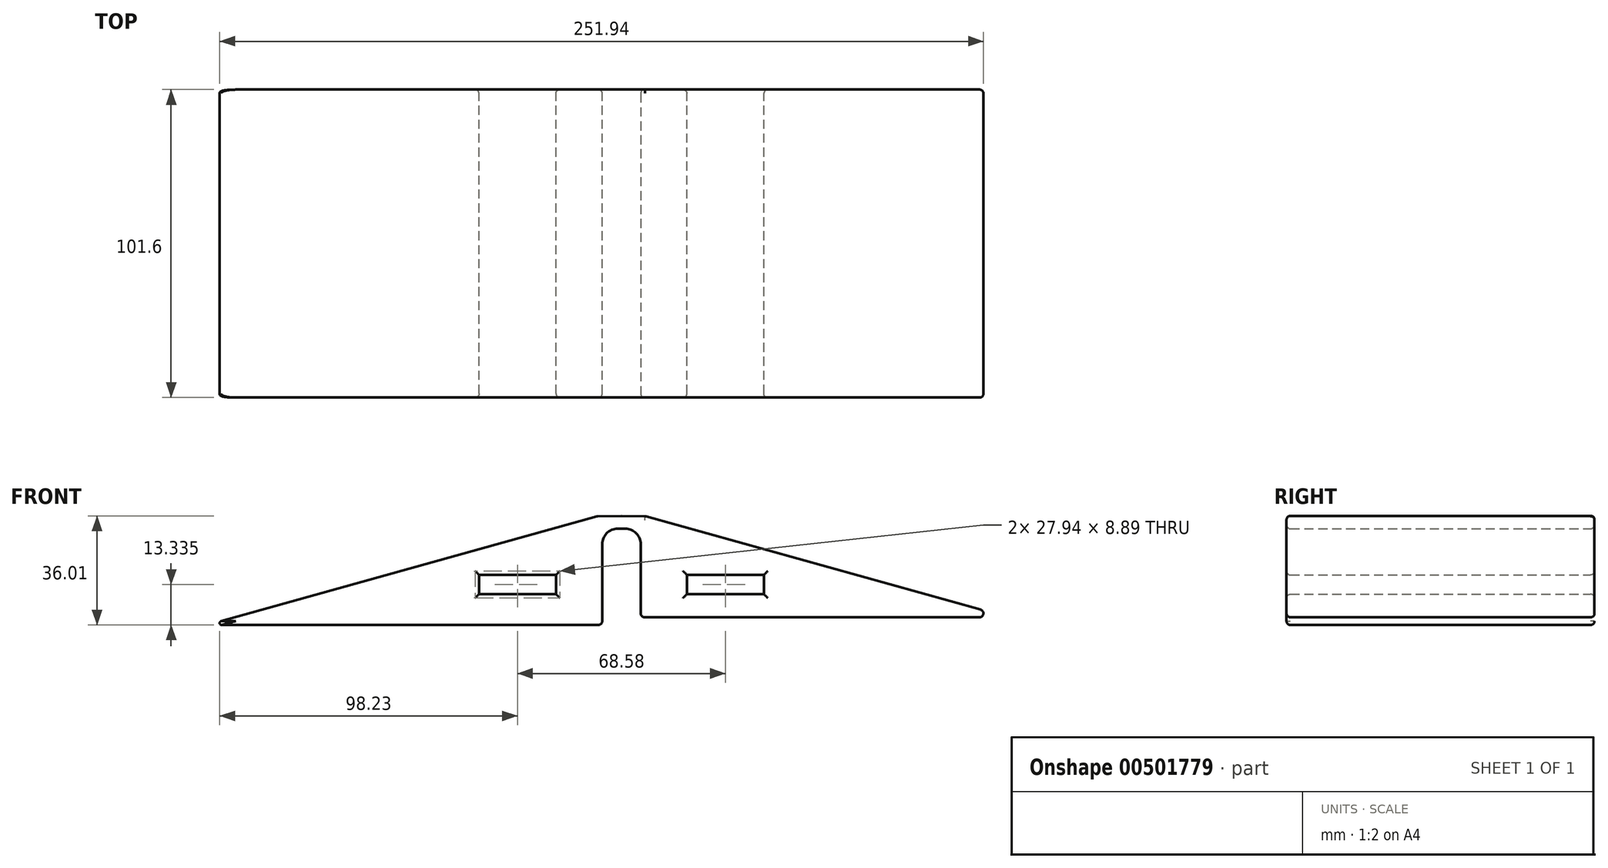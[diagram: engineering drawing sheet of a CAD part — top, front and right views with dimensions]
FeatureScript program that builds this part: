
annotation { "Feature Type Name" : "Feature", "Feature Type Description" : "" }
export const myFeature = defineFeature(function(context is Context, id is Id, definition is map)
    precondition{}
    {
        {
            var Q0;
            Q0=qCreatedBy(makeId("Front.planeOp"),FACE);
            var sketch = newSketch(context, id + "F0", { "sketchPlane" : qUnion([Q0])});
            skLineSegment(sketch, "E0", {"start": v(-6.35, 0) * mm, "end": v(-136.53, 0) * mm});
            skLineSegment(sketch, "E1", {"start": v(-136.53, 0) * mm, "end": v(-7.96, 35.88) * mm});
            skLineSegment(sketch, "E2", {"start": v(0, 36) * mm, "end": v(0, 31.75) * mm});
            skLineSegment(sketch, "E3", {"start": v(-6.35, 0) * mm, "end": v(-6.35, 31.75) * mm});
            skLineSegment(sketch, "E4", {"start": v(-6.35, 31.75) * mm, "end": v(0, 31.75) * mm});
            skLineSegment(sketch, "E5", {"start": v(0, 36) * mm, "end": v(-7.96, 35.88) * mm});
            skPoint(sketch, "E6.orphan", {"position": v(0, 38.1) * mm});
            skPoint(sketch, "E7.orphan", {"position": v(0, 0) * mm});
            skLineSegment(sketch, "E8.bottom", {"start": v(-21.59, 10.16) * mm, "end": v(-47, 10.16) * mm});
            skLineSegment(sketch, "E8.top", {"start": v(-21.59, 16.51) * mm, "end": v(-47, 16.5) * mm});
            skLineSegment(sketch, "E8.left", {"start": v(-21.59, 10.16) * mm, "end": v(-21.59, 16.51) * mm});
            skLineSegment(sketch, "E8.right", {"start": v(-47, 10.16) * mm, "end": v(-47, 16.5) * mm});
            skPoint(sketch, "E8.middle", {"position": v(-34.3, 13.33) * mm});
            skSolve(sketch);
        }
        {
            var Q0;
            Q0=makeQuery(id+"F0.imprint","IMPRINT",FACE,{"disambiguationData":[TD([[makeQuery(id+"F0.imprint","IMPRINT",EDGE,{"derivedFrom":sQuery(id+"F0.wireOp",EDGE,"E0")}),-1.0]])]});
            extrude(context, id + "F1", {"entities" : qUnion([Q0]), "depth" : 101.6 * mm});
        }
        {
            var Q0;
            Q0=makeQuery(id+"F1.opExtrude","SWEPT_BODY",BODY,{"disambiguationData":[OSD([sQuery(id+"F0.wireOp",EDGE,"E0"),sQuery(id+"F0.wireOp",EDGE,"E1"),sQuery(id+"F0.wireOp",EDGE,"E2"),sQuery(id+"F0.wireOp",EDGE,"E3"),sQuery(id+"F0.wireOp",EDGE,"E4"),sQuery(id+"F0.wireOp",EDGE,"E5"),sQuery(id+"F0.wireOp",EDGE,"E8.bottom"),sQuery(id+"F0.wireOp",EDGE,"E8.top"),sQuery(id+"F0.wireOp",EDGE,"E8.left"),sQuery(id+"F0.wireOp",EDGE,"E8.right")])]});
            var Q1;
            Q1=qCreatedBy(makeId("Right.planeOp"),FACE);
            mirror(context, id + "F2", {"operationType" : NewBodyOperationType.ADD, "entities" : qUnion([Q0]), "mirrorPlane" : qUnion([Q1])});
        }
        {
            var Q0;
            Q0=makeQuery(id+"F1.opExtrude","SWEPT_EDGE",EDGE,{"disambiguationData":[OSD([sQuery(id+"F0.wireOp",EDGE,"E0"),sQuery(id+"F0.wireOp",EDGE,"E1")])]});
            var Q1;
            Q1=makeQuery(id+"F2.opPattern","COPY",EDGE,{"derivedFrom":makeQuery(id+"F1.opExtrude","SWEPT_EDGE",EDGE,{"disambiguationData":[OSD([sQuery(id+"F0.wireOp",EDGE,"E0"),sQuery(id+"F0.wireOp",EDGE,"E1")])]}),"instanceName":"1"});
            fillet(context, id + "F3", {"entities" : qUnion([Q0, Q1]), "radius" : 0.64 * mm, "tangentPropagation" : true, "allowEdgeOverflow" : false});
        }
        {
            var Q0;
            Q0=makeQuery(id+"F2.opPattern","COPY",EDGE,{"derivedFrom":makeQuery(id+"F1.opExtrude","SWEPT_EDGE",EDGE,{"disambiguationData":[OSD([sQuery(id+"F0.wireOp",EDGE,"E3"),sQuery(id+"F0.wireOp",EDGE,"E4")])]}),"instanceName":"1"});
            var Q1;
            Q1=makeQuery(id+"F1.opExtrude","SWEPT_EDGE",EDGE,{"disambiguationData":[OSD([sQuery(id+"F0.wireOp",EDGE,"E3"),sQuery(id+"F0.wireOp",EDGE,"E4")])]});
            fillet(context, id + "F4", {"entities" : qUnion([Q0, Q1]), "radius" : 5.08 * mm, "tangentPropagation" : true, "allowEdgeOverflow" : false});
        }
        {
            var Q0;
            {var subQ0=makeQuery(id+"F1.opExtrude","CAP_FACE",FACE,{"disambiguationData":[OSD([sQuery(id+"F0.wireOp",EDGE,"E0"),sQuery(id+"F0.wireOp",EDGE,"E1"),sQuery(id+"F0.wireOp",EDGE,"E2"),sQuery(id+"F0.wireOp",EDGE,"E3"),sQuery(id+"F0.wireOp",EDGE,"E4"),sQuery(id+"F0.wireOp",EDGE,"E5"),sQuery(id+"F0.wireOp",EDGE,"E8.bottom"),sQuery(id+"F0.wireOp",EDGE,"E8.top"),sQuery(id+"F0.wireOp",EDGE,"E8.left"),sQuery(id+"F0.wireOp",EDGE,"E8.right")])],"isStart":false});Q0=makeQuery(id+"F2.boolean.opBoolean","MERGE",FACE,{"derivedFrom":[subQ0,makeQuery(id+"F2.opPattern","COPY",FACE,{"derivedFrom":subQ0,"instanceName":"1"})]});}
            var sketch = newSketch(context, id + "F5", { "sketchPlane" : qUnion([Q0])});
            skPoint(sketch, "E9.0", {"position": v(6.35, 0) * mm});
            skLineSegment(sketch, "E10.bottom", {"start": v(6.35, 0) * mm, "end": v(139.9, 0) * mm});
            skLineSegment(sketch, "E10.top", {"start": v(6.35, 2.54) * mm, "end": v(139.9, 2.54) * mm});
            skLineSegment(sketch, "E10.left", {"start": v(6.35, 0) * mm, "end": v(6.35, 2.54) * mm});
            skLineSegment(sketch, "E10.right", {"start": v(139.9, 0) * mm, "end": v(139.9, 2.54) * mm});
            skSolve(sketch);
        }
        {
            var Q0;
            {var subQ5=sQuery(id+"F5.wireOp",EDGE,"E10.left");Q0=makeQuery(id+"F5.imprint","IMPRINT",FACE,{"disambiguationData":[TD([[makeQuery(id+"F5.imprint","IMPRINT",EDGE,{"derivedFrom":subQ5}),-1.0]])]});}
            extrude(context, id + "F6", {"entities" : qUnion([Q0]), "operationType" : NewBodyOperationType.REMOVE, "endBound" : BoundingType.THROUGH_ALL, "oppositeDirection" : true, "depth" : 25.4 * mm});
        }
        {
            var Q0;
            Q0=makeQuery(id+"F2.opPattern","COPY",FACE,{"derivedFrom":makeQuery(id+"F1.opExtrude","SWEPT_FACE",FACE,{"disambiguationData":[OSD([sQuery(id+"F0.wireOp",EDGE,"E1")])]}),"instanceName":"1"});
            var Q1;
            Q1=makeQuery(id+"F1.opExtrude","SWEPT_FACE",FACE,{"disambiguationData":[OSD([sQuery(id+"F0.wireOp",EDGE,"E1")])]});
            var Q2;
            Q2=makeQuery(id+"F1.opExtrude","SWEPT_FACE",FACE,{"disambiguationData":[OSD([sQuery(id+"F0.wireOp",EDGE,"E5")])]});
            var Q3;
            Q3=makeQuery(id+"F2.opPattern","COPY",FACE,{"derivedFrom":makeQuery(id+"F1.opExtrude","SWEPT_FACE",FACE,{"disambiguationData":[OSD([sQuery(id+"F0.wireOp",EDGE,"E5")])]}),"instanceName":"1"});
            var Q4;
            {var subQ0=makeQuery(id+"F1.opExtrude","CAP_FACE",FACE,{"disambiguationData":[OSD([sQuery(id+"F0.wireOp",EDGE,"E0"),sQuery(id+"F0.wireOp",EDGE,"E1"),sQuery(id+"F0.wireOp",EDGE,"E2"),sQuery(id+"F0.wireOp",EDGE,"E3"),sQuery(id+"F0.wireOp",EDGE,"E4"),sQuery(id+"F0.wireOp",EDGE,"E5"),sQuery(id+"F0.wireOp",EDGE,"E8.bottom"),sQuery(id+"F0.wireOp",EDGE,"E8.top"),sQuery(id+"F0.wireOp",EDGE,"E8.left"),sQuery(id+"F0.wireOp",EDGE,"E8.right")])],"isStart":true});Q4=makeQuery(id+"F2.boolean.opBoolean","MERGE",FACE,{"derivedFrom":[subQ0,makeQuery(id+"F2.opPattern","COPY",FACE,{"derivedFrom":subQ0,"instanceName":"1"})]});}
            var Q5;
            {var subQ0=makeQuery(id+"F1.opExtrude","CAP_FACE",FACE,{"disambiguationData":[OSD([sQuery(id+"F0.wireOp",EDGE,"E0"),sQuery(id+"F0.wireOp",EDGE,"E1"),sQuery(id+"F0.wireOp",EDGE,"E2"),sQuery(id+"F0.wireOp",EDGE,"E3"),sQuery(id+"F0.wireOp",EDGE,"E4"),sQuery(id+"F0.wireOp",EDGE,"E5"),sQuery(id+"F0.wireOp",EDGE,"E8.bottom"),sQuery(id+"F0.wireOp",EDGE,"E8.top"),sQuery(id+"F0.wireOp",EDGE,"E8.left"),sQuery(id+"F0.wireOp",EDGE,"E8.right")])],"isStart":false});Q5=makeQuery(id+"F2.boolean.opBoolean","MERGE",FACE,{"derivedFrom":[subQ0,makeQuery(id+"F2.opPattern","COPY",FACE,{"derivedFrom":subQ0,"instanceName":"1"})]});}
            var Q6;
            Q6=makeQuery(id+"F6.boolean.opBoolean","COPY",FACE,{"derivedFrom":makeQuery(id+"F6.opExtrude","SWEPT_FACE",FACE,{"disambiguationData":[OSD([sQuery(id+"F5.wireOp",EDGE,"E10.top")])]})});
            var Q7;
            Q7=makeQuery(id+"F1.opExtrude","SWEPT_FACE",FACE,{"disambiguationData":[OSD([sQuery(id+"F0.wireOp",EDGE,"E0")])]});
            fillet(context, id + "F7", {"entities" : qUnion([Q0, Q1, Q2, Q3, Q4, Q5, Q6, Q7]), "radius" : 1.27 * mm, "tangentPropagation" : true, "allowEdgeOverflow" : false});
        }
    });
